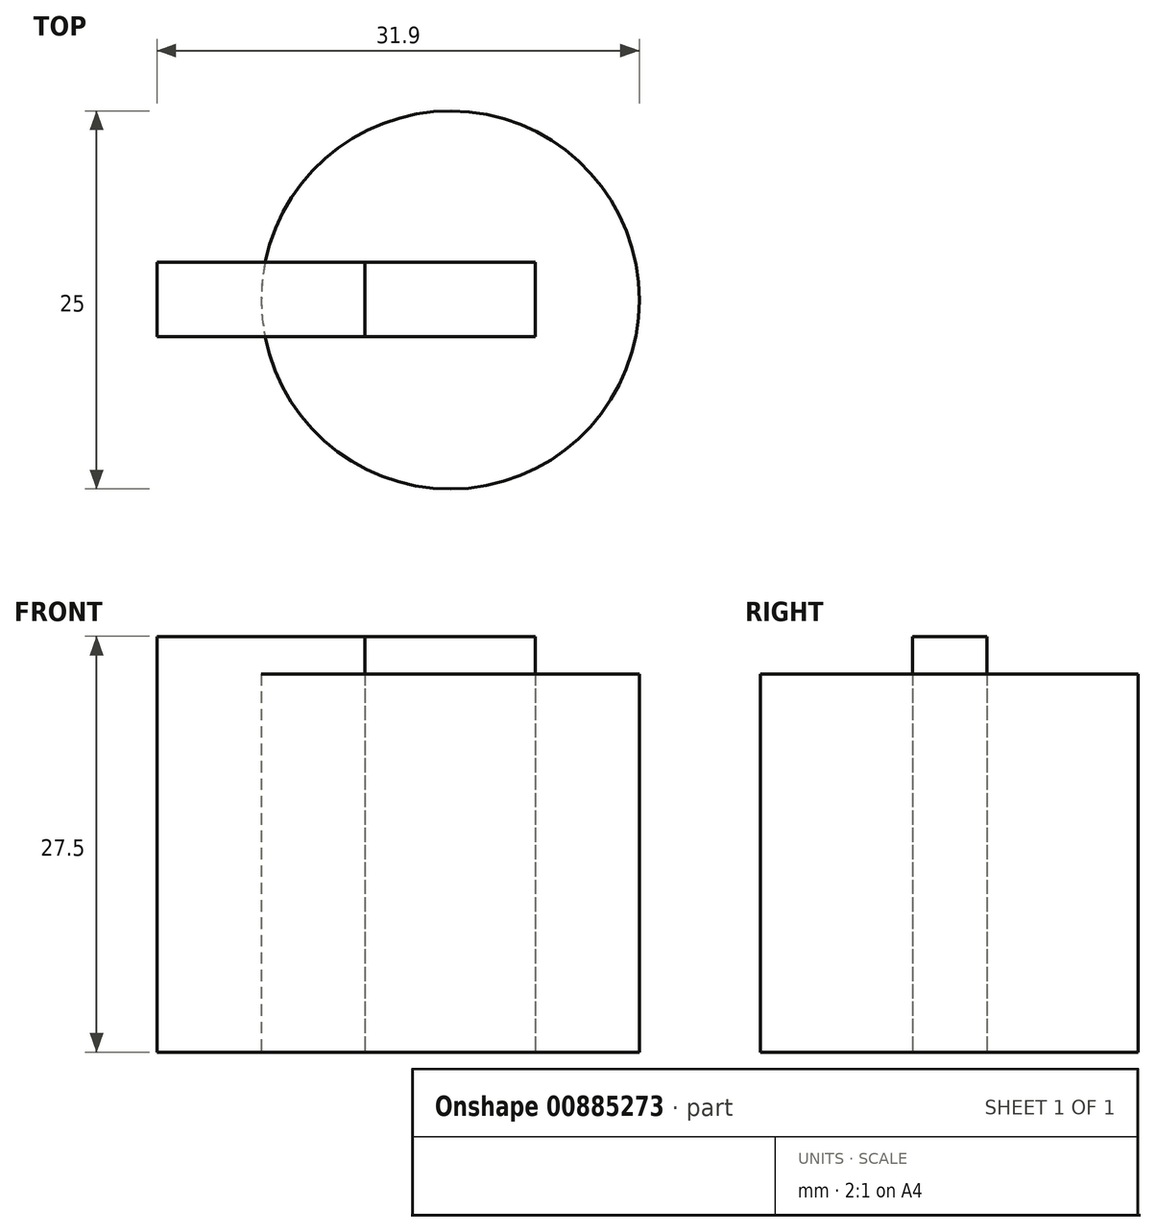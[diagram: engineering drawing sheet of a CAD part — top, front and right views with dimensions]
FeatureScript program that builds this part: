
annotation { "Feature Type Name" : "Feature", "Feature Type Description" : "" }
export const myFeature = defineFeature(function(context is Context, id is Id, definition is map)
    precondition{}
    {
        {
            var Q0;
            Q0=qCreatedBy(makeId("Top.planeOp"),FACE);
            var sketch = newSketch(context, id + "F0", { "sketchPlane" : qUnion([Q0])});
            skCircle(sketch, "E0", {"center": v(0, 0) * mm, "radius": 12.5 * mm});
            skSolve(sketch);
        }
        {
            var Q0;
            Q0=makeQuery(id+"F0.imprint","IMPRINT",FACE,{"disambiguationData":[TD([[makeQuery(id+"F0.imprint","IMPRINT",EDGE,{"derivedFrom":sQuery(id+"F0.wireOp",EDGE,"E0")}),1.0]])]});
            var sketch = newSketch(context, id + "F1", { "sketchPlane" : qUnion([Q0])});
            skLineSegment(sketch, "E1.bottom", {"start": v(-5.65, -2.41) * mm, "end": v(5.6, -2.41) * mm});
            skLineSegment(sketch, "E1.top", {"start": v(-5.65, 2.49) * mm, "end": v(5.6, 2.49) * mm});
            skLineSegment(sketch, "E1.left", {"start": v(-5.65, -2.41) * mm, "end": v(-5.65, 2.49) * mm});
            skLineSegment(sketch, "E1.right", {"start": v(5.6, -2.41) * mm, "end": v(5.6, 2.49) * mm});
            skPoint(sketch, "E1.middle", {"position": v(-0.02, 0.04) * mm});
            skSolve(sketch);
        }
        {
            var Q0;
            Q0=makeQuery(id+"F1.imprint","IMPRINT",FACE,{"disambiguationData":[TD([[makeQuery(id+"F1.imprint","IMPRINT",EDGE,{"derivedFrom":sQuery(id+"F1.wireOp",EDGE,"E1.bottom")}),1.0]])]});
            var sketch = newSketch(context, id + "F2", { "sketchPlane" : qUnion([Q0])});
            skSolve(sketch);
        }
        {
            var Q0;
            Q0=makeQuery(id+"F0.imprint","IMPRINT",FACE,{"disambiguationData":[TD([[makeQuery(id+"F0.imprint","IMPRINT",EDGE,{"derivedFrom":sQuery(id+"F0.wireOp",EDGE,"E0")}),1.0]])]});
            var Q1;
            Q1=makeQuery(id+"F1.imprint","IMPRINT",FACE,{"disambiguationData":[TD([[makeQuery(id+"F1.imprint","IMPRINT",EDGE,{"derivedFrom":sQuery(id+"F1.wireOp",EDGE,"E1.bottom")}),1.0]])]});
            extrude(context, id + "F3", {"entities" : qUnion([Q0, Q1]), "depth" : 25 * mm, "offsetDistance" : 25 * mm});
        }
        {
            var Q0;
            Q0=makeQuery(id+"F2.imprint","IMPRINT",FACE,{"disambiguationData":[TD([[makeQuery(id+"F2.imprint","IMPRINT",EDGE,{"derivedFrom":makeQuery(id+"F1.imprint","IMPRINT",EDGE,{"derivedFrom":sQuery(id+"F1.wireOp",EDGE,"E1.bottom")})}),1.0]])]});
            extrude(context, id + "F4", {"entities" : qUnion([Q0]), "depth" : 27.5 * mm, "offsetDistance" : 25 * mm});
        }
        {
            var Q0;
            Q0=makeQuery(id+"F4.opExtrude","SWEPT_FACE",FACE,{"disambiguationData":[OSD([sQuery(id+"F1.wireOp",EDGE,"E1.right")])]});
            extrude(context, id + "F5", {"entities" : qUnion([Q0]), "oppositeDirection" : true, "depth" : 25 * mm, "offsetDistance" : 25 * mm});
        }
    });
